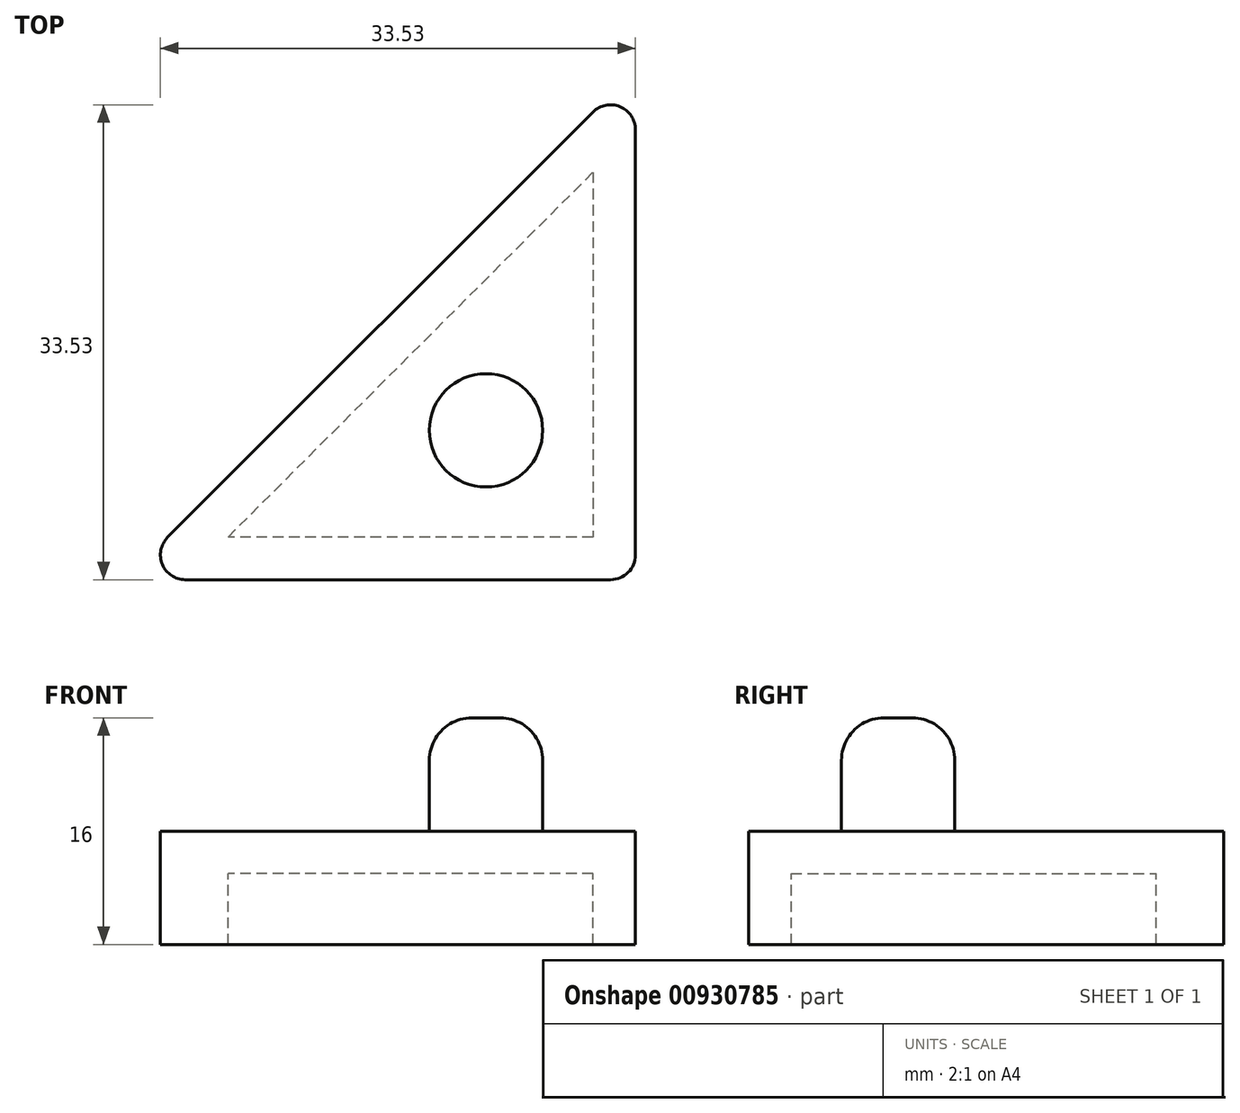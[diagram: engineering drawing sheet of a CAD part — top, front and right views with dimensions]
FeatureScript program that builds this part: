
annotation { "Feature Type Name" : "Feature", "Feature Type Description" : "" }
export const myFeature = defineFeature(function(context is Context, id is Id, definition is map)
    precondition{}
    {
        {
            var Q0;
            Q0=qCreatedBy(makeId("Top.planeOp"),FACE);
            var sketch = newSketch(context, id + "F0", { "sketchPlane" : qUnion([Q0])});
            skLineSegment(sketch, "E0", {"start": v(-36, 0) * mm, "end": v(0, 0) * mm});
            skLineSegment(sketch, "E1", {"start": v(0, 0) * mm, "end": v(0, 36) * mm});
            skLineSegment(sketch, "E2", {"start": v(0, 36) * mm, "end": v(-36, 0) * mm});
            skCircle(sketch, "E3", {"center": v(-31.78, 1.75) * mm, "radius": 1.75 * mm});
            skCircle(sketch, "E4", {"center": v(-1.75, 1.75) * mm, "radius": 1.75 * mm});
            skCircle(sketch, "E5", {"center": v(-1.75, 31.78) * mm, "radius": 1.75 * mm});
            skCircle(sketch, "E6", {"center": v(-10.54, 10.54) * mm, "radius": 4 * mm});
            skLineSegment(sketch, "E7", {"start": v(-13.37, 13.37) * mm, "end": v(-18, 18) * mm, "construction": true});
            skLineSegment(sketch, "E8", {"start": v(0, 10.54) * mm, "end": v(-6.54, 10.54) * mm, "construction": true});
            skLineSegment(sketch, "E9", {"start": v(-10.54, 6.54) * mm, "end": v(-10.54, 0) * mm, "construction": true});
            skLineSegment(sketch, "E10", {"start": v(-28.76, 3) * mm, "end": v(-3, 28.76) * mm});
            skLineSegment(sketch, "E11", {"start": v(-3, 28.76) * mm, "end": v(-3, 3) * mm});
            skLineSegment(sketch, "E12", {"start": v(-3, 3) * mm, "end": v(-28.76, 3) * mm});
            skLineSegment(sketch, "E13", {"start": v(-18.8, 0) * mm, "end": v(-18.8, 3) * mm, "construction": true});
            skLineSegment(sketch, "E14", {"start": v(-22.16, 9.6) * mm, "end": v(-24.28, 11.72) * mm, "construction": true});
            skLineSegment(sketch, "E15", {"start": v(-3, 18) * mm, "end": v(0, 18) * mm, "construction": true});
            skPoint(sketch, "E15.startSnap0", {"position": v(0, 18) * mm});
            skPoint(sketch, "E15.startSnap1", {"position": v(-3, 15.88) * mm});
            skLineSegment(sketch, "E16", {"start": v(-31.97, 33.53) * mm, "end": v(29.29, 33.53) * mm, "construction": true});
            skSolve(sketch);
        }
        {
            var Q0;
            Q0=makeQuery(id+"F0.imprint","IMPRINT",FACE,{"disambiguationData":[TD([[makeQuery(id+"F0.imprint","IMPRINT",EDGE,{"derivedFrom":sQuery(id+"F0.wireOp",EDGE,"E6")}),1.0]])]});
            extrude(context, id + "F1", {"entities" : qUnion([Q0]), "depth" : 11 * mm, "offsetDistance" : 25 * mm});
        }
        {
            var Q0;
            Q0=makeQuery(id+"F0.imprint","IMPRINT",FACE,{"disambiguationData":[TD([[makeQuery(id+"F0.imprint","IMPRINT",EDGE,{"derivedFrom":sQuery(id+"F0.wireOp",EDGE,"E6")}),-1.0]])]});
            var Q1;
            {var subQ0=sQuery(id+"F0.wireOp",EDGE,"E3");var subQ1=makeQuery(id+"F0.imprint","INTERSECT",VERTEX,{"derivedFrom":[sQuery(id+"F0.wireOp",EDGE,"E0"),subQ0]});Q1=makeQuery(id+"F0.imprint","IMPRINT",FACE,{"disambiguationData":[TD([[makeQuery(id+"F0.imprint","IMPRINT",EDGE,{"disambiguationData":[TD([[subQ1,1.0]])],"derivedFrom":subQ0}),1.0]])]});}
            var Q2;
            {var subQ0=sQuery(id+"F0.wireOp",EDGE,"E4");var subQ1=makeQuery(id+"F0.imprint","INTERSECT",VERTEX,{"derivedFrom":[sQuery(id+"F0.wireOp",EDGE,"E0"),subQ0]});Q2=makeQuery(id+"F0.imprint","IMPRINT",FACE,{"disambiguationData":[TD([[makeQuery(id+"F0.imprint","IMPRINT",EDGE,{"disambiguationData":[TD([[subQ1,1.0]])],"derivedFrom":subQ0}),1.0]])]});}
            var Q3;
            {var subQ0=sQuery(id+"F0.wireOp",EDGE,"E5");var subQ1=makeQuery(id+"F0.imprint","INTERSECT",VERTEX,{"derivedFrom":[sQuery(id+"F0.wireOp",EDGE,"E1"),subQ0]});Q3=makeQuery(id+"F0.imprint","IMPRINT",FACE,{"disambiguationData":[TD([[makeQuery(id+"F0.imprint","IMPRINT",EDGE,{"disambiguationData":[TD([[subQ1,-1.0]])],"derivedFrom":subQ0}),1.0]])]});}
            var Q4;
            {var subQ7=sQuery(id+"F0.wireOp",EDGE,"E10");Q4=makeQuery(id+"F0.imprint","IMPRINT",FACE,{"disambiguationData":[TD([[makeQuery(id+"F0.imprint","IMPRINT",EDGE,{"derivedFrom":subQ7}),1.0]])]});}
            var Q5;
            {var subQ0=sQuery(id+"F0.wireOp",EDGE,"E11");var subQ1=sQuery(id+"F0.wireOp",EDGE,"E4");var subQ2=makeQuery(id+"F0.imprint","INTERSECT",VERTEX,{"derivedFrom":[subQ1,subQ0]});Q5=makeQuery(id+"F0.imprint","IMPRINT",FACE,{"disambiguationData":[TD([[makeQuery(id+"F0.imprint","IMPRINT",EDGE,{"disambiguationData":[TD([[subQ2,-1.0]])],"derivedFrom":subQ1}),1.0]])]});}
            extrude(context, id + "F2", {"entities" : qUnion([Q0, Q1, Q2, Q3, Q4, Q5]), "operationType" : NewBodyOperationType.ADD, "depth" : 3 * mm, "offsetDistance" : 25 * mm});
        }
        {
            var Q0;
            {var subQ7=sQuery(id+"F0.wireOp",EDGE,"E10");Q0=makeQuery(id+"F0.imprint","IMPRINT",FACE,{"disambiguationData":[TD([[makeQuery(id+"F0.imprint","IMPRINT",EDGE,{"derivedFrom":subQ7}),1.0]])]});}
            var Q1;
            {var subQ3=sQuery(id+"F0.wireOp",EDGE,"E4");var subQ6=makeQuery(id+"F0.imprint","INTERSECT",VERTEX,{"derivedFrom":[sQuery(id+"F0.wireOp",EDGE,"E1"),subQ3]});Q1=makeQuery(id+"F0.imprint","IMPRINT",FACE,{"disambiguationData":[TD([[makeQuery(id+"F0.imprint","IMPRINT",EDGE,{"disambiguationData":[TD([[subQ6,-1.0]])],"derivedFrom":subQ3}),1.0]])]});}
            var Q2;
            {var subQ0=sQuery(id+"F0.wireOp",EDGE,"E5");var subQ1=makeQuery(id+"F0.imprint","INTERSECT",VERTEX,{"derivedFrom":[sQuery(id+"F0.wireOp",EDGE,"E1"),subQ0]});Q2=makeQuery(id+"F0.imprint","IMPRINT",FACE,{"disambiguationData":[TD([[makeQuery(id+"F0.imprint","IMPRINT",EDGE,{"disambiguationData":[TD([[subQ1,-1.0]])],"derivedFrom":subQ0}),1.0]])]});}
            var Q3;
            {var subQ0=sQuery(id+"F0.wireOp",EDGE,"E3");var subQ1=makeQuery(id+"F0.imprint","INTERSECT",VERTEX,{"derivedFrom":[sQuery(id+"F0.wireOp",EDGE,"E0"),subQ0]});Q3=makeQuery(id+"F0.imprint","IMPRINT",FACE,{"disambiguationData":[TD([[makeQuery(id+"F0.imprint","IMPRINT",EDGE,{"disambiguationData":[TD([[subQ1,1.0]])],"derivedFrom":subQ0}),1.0]])]});}
            extrude(context, id + "F3", {"entities" : qUnion([Q0, Q1, Q2, Q3]), "operationType" : NewBodyOperationType.ADD, "depth" : -5 * mm, "offsetDistance" : 25 * mm});
        }
        {
            var Q0;
            Q0=makeQuery(id+"F1.opExtrude","CAP_EDGE",EDGE,{"disambiguationData":[OSD([sQuery(id+"F0.wireOp",EDGE,"E6")])],"isStart":false});
            fillet(context, id + "F4", {"entities" : qUnion([Q0]), "radius" : 3 * mm, "tangentPropagation" : true, "allowEdgeOverflow" : false});
        }
    });
